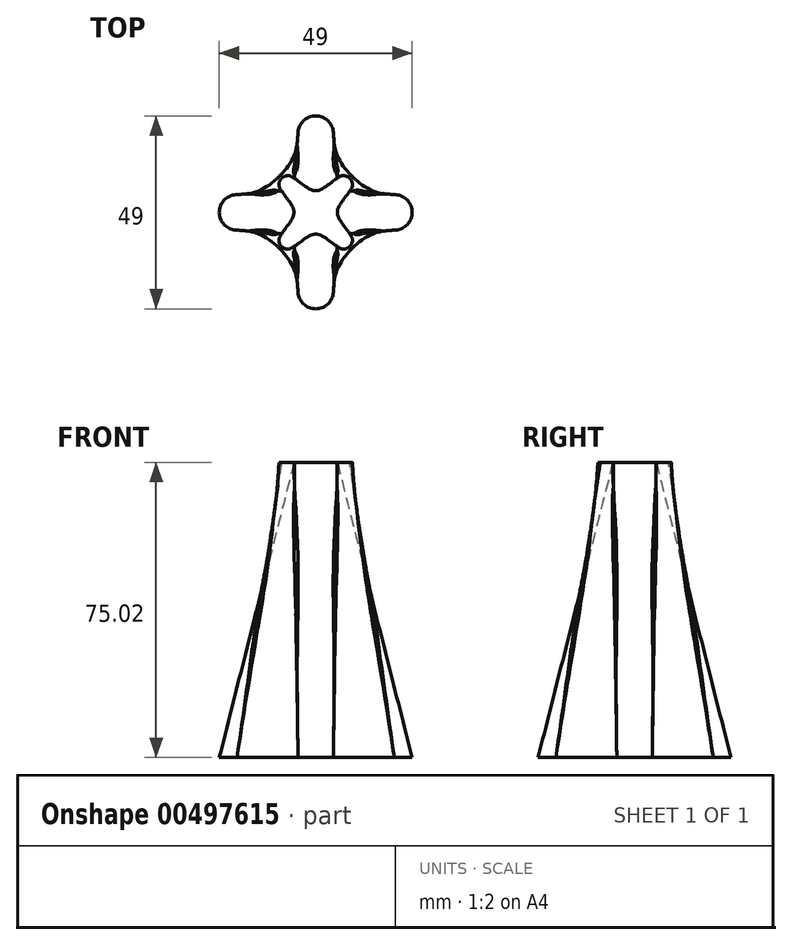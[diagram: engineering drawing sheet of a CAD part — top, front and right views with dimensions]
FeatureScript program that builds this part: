
annotation { "Feature Type Name" : "Feature", "Feature Type Description" : "" }
export const myFeature = defineFeature(function(context is Context, id is Id, definition is map)
    precondition{}
    {
        {
            var Q0;
            Q0=qCreatedBy(makeId("Top.planeOp"),FACE);
            var sketch = newSketch(context, id + "F0", { "sketchPlane" : qUnion([Q0])});
            skLineSegment(sketch, "E0", {"start": v(0, 0) * mm, "end": v(0, 20) * mm});
            skArc(sketch, "E1", {"start": v(4.5, 20) * mm, "mid": v(0, 24.5) * mm, "end": v(-4.5, 20) * mm});
            skArc(sketch, "E2", {"start": v(20, -4.5) * mm, "mid": v(24.5, 0) * mm, "end": v(20, 4.5) * mm});
            skArc(sketch, "E3.MirrorC", {"start": v(-20, -4.5) * mm, "mid": v(-24.5, 0) * mm, "end": v(-20, 4.5) * mm});
            skArc(sketch, "E4.MirrorC", {"start": v(4.5, -20) * mm, "mid": v(0, -24.5) * mm, "end": v(-4.5, -20) * mm});
            skLineSegment(sketch, "E5", {"start": v(5, 5) * mm, "end": v(10, 0) * mm});
            skPoint(sketch, "E6", {"position": v(4.5, 20) * mm});
            skPoint(sketch, "E7", {"position": v(20, 4.5) * mm});
            skFitSpline(sketch, "E8", {"points": [v(4.5, 20) * mm, v(9.2, 9.2) * mm, v(20, 4.5) * mm], "startDerivative": vector(-0.04, -31.04) * mm, "endDerivative": vector(31.04, 0.04) * mm});
            skPoint(sketch, "E9.MirrorP", {"position": v(-4.5, 20) * mm});
            skPoint(sketch, "E10.MirrorP", {"position": v(-20, 4.5) * mm});
            skFitSpline(sketch, "E11", {"points": [v(-20, 4.5) * mm, v(-9.2, 9.2) * mm, v(-4.5, 20) * mm], "startDerivative": vector(31.04, -0.04) * mm, "endDerivative": vector(-0.04, 31.04) * mm});
            skFitSpline(sketch, "E12.MirrorCS", {"points": [v(-20, -4.5) * mm, v(-9.2, -9.2) * mm, v(-4.5, -20) * mm], "startDerivative": vector(31.04, 0.04) * mm, "endDerivative": vector(-0.04, -31.04) * mm});
            skFitSpline(sketch, "E13.MirrorCS", {"points": [v(4.5, -20) * mm, v(9.2, -9.2) * mm, v(20, -4.5) * mm], "startDerivative": vector(-0.04, 31.04) * mm, "endDerivative": vector(31.04, -0.04) * mm});
            skPoint(sketch, "E14.orphan", {"position": v(0, 10) * mm});
            skSolve(sketch);
        }
        {
            var Q0;
            Q0=qCreatedBy(makeId("Top.planeOp"),FACE);
            cPlane(context, id + "F1", {"entities" : qUnion([Q0]), "cplaneType" : CPlaneType.OFFSET, "offset" : 75 * mm, "width" : 150 * mm, "height" : 150 * mm});
        }
        {
            var Q0;
            Q0=qCreatedBy(id+"F1.planeOp",FACE);
            var sketch = newSketch(context, id + "F2", { "sketchPlane" : qUnion([Q0])});
            skLineSegment(sketch, "E15", {"start": v(3.54, -3.54) * mm, "end": v(7.07, -7.07) * mm});
            skLineSegment(sketch, "E16", {"start": v(3.54, -3.54) * mm, "end": v(-3.54, -3.54) * mm});
            skArc(sketch, "E17", {"start": v(5.48, -8.66) * mm, "mid": v(8.66, -8.66) * mm, "end": v(8.66, -5.48) * mm});
            skArc(sketch, "E18", {"start": v(-8.66, -5.48) * mm, "mid": v(-8.66, -8.66) * mm, "end": v(-5.48, -8.66) * mm});
            skPoint(sketch, "E19", {"position": v(5.48, -8.66) * mm});
            skPoint(sketch, "E20", {"position": v(-5.48, -8.66) * mm});
            skFitSpline(sketch, "E21", {"points": [v(5.48, -8.66) * mm, v(0, -5.5) * mm, v(-5.48, -8.66) * mm], "startDerivative": vector(-10.96, 6.49) * mm, "endDerivative": vector(-10.96, -6.49) * mm});
            skArc(sketch, "E22.MirrorC", {"start": v(5.48, 8.66) * mm, "mid": v(8.66, 8.66) * mm, "end": v(8.66, 5.48) * mm});
            skFitSpline(sketch, "E23.MirrorCS", {"points": [v(5.48, 8.66) * mm, v(0, 5.5) * mm, v(-5.48, 8.66) * mm], "startDerivative": vector(-10.96, -6.49) * mm, "endDerivative": vector(-10.96, 6.49) * mm});
            skArc(sketch, "E24.MirrorC", {"start": v(-8.66, 5.48) * mm, "mid": v(-8.66, 8.66) * mm, "end": v(-5.48, 8.66) * mm});
            skFitSpline(sketch, "E25.MirrorCS", {"points": [v(-8.66, -5.48) * mm, v(-5.5, 0) * mm, v(-8.66, 5.48) * mm], "startDerivative": vector(6.49, 10.96) * mm, "endDerivative": vector(-6.49, 10.96) * mm});
            skFitSpline(sketch, "E26.MirrorCS", {"points": [v(8.66, -5.48) * mm, v(5.5, 0) * mm, v(8.66, 5.48) * mm], "startDerivative": vector(-6.49, 10.96) * mm, "endDerivative": vector(6.49, 10.96) * mm});
            skPoint(sketch, "E27.MirrorCS.start.orphan", {"position": v(0, 0) * mm});
            skLineSegment(sketch, "E28.0", {"start": v(7.07, -7.07) * mm, "end": v(5.48, -8.66) * mm, "construction": true});
            skLineSegment(sketch, "E29.0", {"start": v(-7.07, -7.07) * mm, "end": v(-5.48, -8.66) * mm, "construction": true});
            skSolve(sketch);
        }
        {
            var Q0;
            {var subQ1=sQuery(id+"F0.wireOp",EDGE,"E1");Q0=makeQuery(id+"F0.imprint","IMPRINT",FACE,{"disambiguationData":[TD([[makeQuery(id+"F0.imprint","IMPRINT",EDGE,{"derivedFrom":subQ1}),1.0]])]});}
            var Q1;
            {var subQ3=sQuery(id+"F2.wireOp",EDGE,"E17");Q1=makeQuery(id+"F2.imprint","IMPRINT",FACE,{"disambiguationData":[TD([[makeQuery(id+"F2.imprint","IMPRINT",EDGE,{"derivedFrom":subQ3}),1.0]])]});}
            var Q2;
            Q2=sQuery(id+"F0.wireOp",VERTEX,"E8.1.internal");
            var Q3;
            Q3=sQuery(id+"F2.wireOp",VERTEX,"fZQEgL5u-Hg5Y-vtmR-KdhO-cswhtPvZJIKj.end");
            loft(context, id + "F3", {"sheetProfilesArray" : [{ "sheetProfileEntities" : qUnion([Q0]) }, { "sheetProfileEntities" : qUnion([Q1]) }], "connections" : [{ "connectionEntities" : qUnion([Q2, Q3]), "connectionEdgeQueries" : qUnion([]), "connectionEdgeParameters" : [] }]});
        }
        {
            var Q0;
            Q0=makeQuery(id+"F3.opLoft","SWEPT_EDGE",EDGE,{"disambiguationData":[OSD([sQuery(id+"F0.wireOp",EDGE,"E4.MirrorC"),sQuery(id+"F0.wireOp",EDGE,"E13.MirrorCS"),sQuery(id+"F2.wireOp",EDGE,"E17"),sQuery(id+"F2.wireOp",EDGE,"E21")])]});
            var Q1;
            Q1=makeQuery(id+"F3.opLoft","SWEPT_EDGE",EDGE,{"disambiguationData":[OSD([sQuery(id+"F0.wireOp",EDGE,"E2"),sQuery(id+"F0.wireOp",EDGE,"E13.MirrorCS"),sQuery(id+"F2.wireOp",EDGE,"E17"),sQuery(id+"F2.wireOp",EDGE,"E26.MirrorCS")])]});
            var Q2;
            Q2=makeQuery(id+"F3.opLoft","SWEPT_EDGE",EDGE,{"disambiguationData":[OSD([sQuery(id+"F0.wireOp",EDGE,"E2"),sQuery(id+"F0.wireOp",EDGE,"E8"),sQuery(id+"F2.wireOp",EDGE,"E22.MirrorC"),sQuery(id+"F2.wireOp",EDGE,"E26.MirrorCS")])]});
            fillet(context, id + "F4", {"entities" : qUnion([Q0, Q1, Q2]), "radius" : 1 * mm, "tangentPropagation" : true, "allowEdgeOverflow" : false});
        }
        {
            var Q0;
            Q0=makeQuery(id+"F3.opLoft","SWEPT_EDGE",EDGE,{"disambiguationData":[OSD([sQuery(id+"F0.wireOp",EDGE,"E1"),sQuery(id+"F0.wireOp",EDGE,"E8"),sQuery(id+"F2.wireOp",EDGE,"E22.MirrorC"),sQuery(id+"F2.wireOp",EDGE,"E23.MirrorCS")])]});
            var Q1;
            Q1=makeQuery(id+"F3.opLoft","SWEPT_EDGE",EDGE,{"disambiguationData":[OSD([sQuery(id+"F0.wireOp",EDGE,"E1"),sQuery(id+"F0.wireOp",EDGE,"E11"),sQuery(id+"F2.wireOp",EDGE,"E23.MirrorCS"),sQuery(id+"F2.wireOp",EDGE,"E24.MirrorC")])]});
            var Q2;
            Q2=makeQuery(id+"F3.opLoft","SWEPT_EDGE",EDGE,{"disambiguationData":[OSD([sQuery(id+"F0.wireOp",EDGE,"E3.MirrorC"),sQuery(id+"F0.wireOp",EDGE,"E11"),sQuery(id+"F2.wireOp",EDGE,"E24.MirrorC"),sQuery(id+"F2.wireOp",EDGE,"E25.MirrorCS")])]});
            fillet(context, id + "F5", {"entities" : qUnion([Q0, Q1, Q2]), "radius" : 1 * mm, "tangentPropagation" : true, "allowEdgeOverflow" : false});
        }
        {
            var Q0;
            Q0=makeQuery(id+"F3.opLoft","SWEPT_EDGE",EDGE,{"disambiguationData":[OSD([sQuery(id+"F0.wireOp",EDGE,"E4.MirrorC"),sQuery(id+"F0.wireOp",EDGE,"E12.MirrorCS"),sQuery(id+"F2.wireOp",EDGE,"E18"),sQuery(id+"F2.wireOp",EDGE,"E21")])]});
            var Q1;
            Q1=makeQuery(id+"F3.opLoft","SWEPT_EDGE",EDGE,{"disambiguationData":[OSD([sQuery(id+"F0.wireOp",EDGE,"E3.MirrorC"),sQuery(id+"F0.wireOp",EDGE,"E12.MirrorCS"),sQuery(id+"F2.wireOp",EDGE,"E18"),sQuery(id+"F2.wireOp",EDGE,"E25.MirrorCS")])]});
            fillet(context, id + "F6", {"entities" : qUnion([Q0, Q1]), "radius" : 1 * mm, "tangentPropagation" : true, "allowEdgeOverflow" : false});
        }
    });
